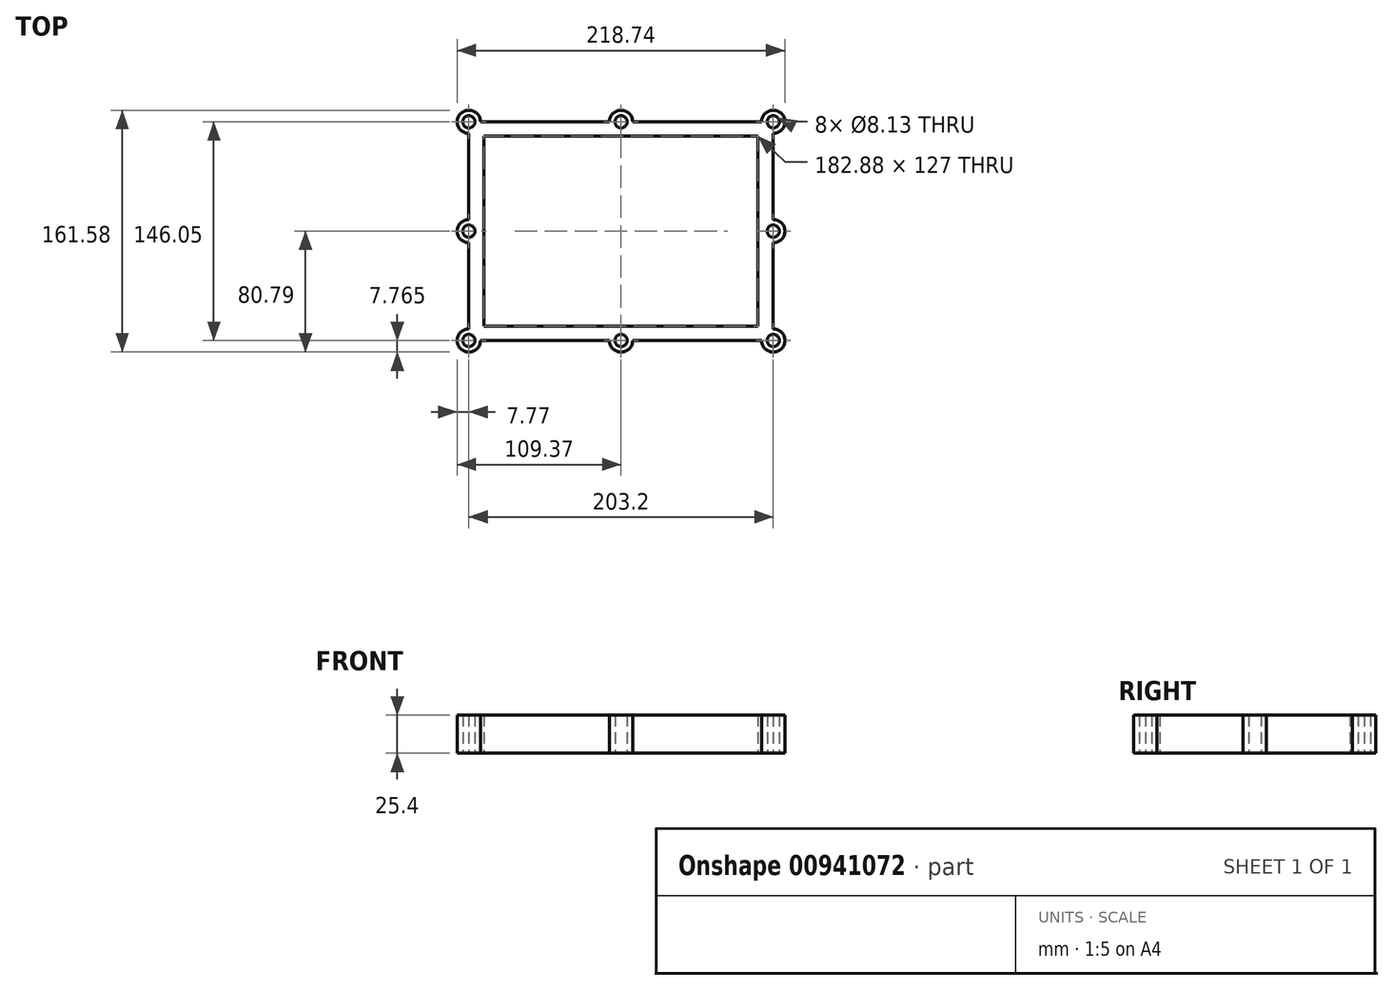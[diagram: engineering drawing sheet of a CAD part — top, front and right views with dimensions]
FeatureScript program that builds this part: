
annotation { "Feature Type Name" : "Feature", "Feature Type Description" : "" }
export const myFeature = defineFeature(function(context is Context, id is Id, definition is map)
    precondition{}
    {
        {
            var Q0;
            Q0=qCreatedBy(makeId("Top.planeOp"),FACE);
            var sketch = newSketch(context, id + "F0", { "sketchPlane" : qUnion([Q0])});
            skLineSegment(sketch, "E0.bottom", {"start": v(-101.6, 73.03) * mm, "end": v(101.6, 73.03) * mm});
            skLineSegment(sketch, "E0.top", {"start": v(-101.6, -73.03) * mm, "end": v(101.6, -73.03) * mm});
            skLineSegment(sketch, "E0.left", {"start": v(-101.6, 73.02) * mm, "end": v(-101.6, -73.03) * mm});
            skLineSegment(sketch, "E0.right", {"start": v(101.6, 73.03) * mm, "end": v(101.6, -73.02) * mm});
            skLineSegment(sketch, "E1", {"start": v(-101.6, 0) * mm, "end": v(101.6, 0) * mm, "construction": true});
            skLineSegment(sketch, "E2", {"start": v(0, 73.03) * mm, "end": v(0, -73.03) * mm, "construction": true});
            skPoint(sketch, "E2.startSnap0", {"position": v(0, 73.02) * mm});
            skCircle(sketch, "E3", {"center": v(101.6, -73.03) * mm, "radius": 7.77 * mm});
            skCircle(sketch, "E4", {"center": v(101.6, -73.03) * mm, "radius": 4.06 * mm});
            skCircle(sketch, "E5", {"center": v(101.6, 0) * mm, "radius": 7.77 * mm});
            skCircle(sketch, "E6", {"center": v(101.6, 0) * mm, "radius": 4.06 * mm});
            skCircle(sketch, "E7", {"center": v(101.6, 73.03) * mm, "radius": 7.77 * mm});
            skCircle(sketch, "E8", {"center": v(101.6, 73.03) * mm, "radius": 4.06 * mm});
            skCircle(sketch, "E9", {"center": v(0, 73.03) * mm, "radius": 7.77 * mm});
            skCircle(sketch, "E10", {"center": v(0, 73.03) * mm, "radius": 4.06 * mm});
            skCircle(sketch, "E11", {"center": v(-101.6, 73.03) * mm, "radius": 7.77 * mm});
            skCircle(sketch, "E12", {"center": v(-101.6, 73.03) * mm, "radius": 4.06 * mm});
            skCircle(sketch, "E13", {"center": v(-101.6, 0) * mm, "radius": 7.77 * mm});
            skCircle(sketch, "E14", {"center": v(-101.6, 0) * mm, "radius": 4.06 * mm});
            skCircle(sketch, "E15", {"center": v(-101.6, -73.03) * mm, "radius": 7.77 * mm});
            skCircle(sketch, "E16", {"center": v(-101.6, -73.03) * mm, "radius": 4.06 * mm});
            skCircle(sketch, "E17", {"center": v(0, -73.03) * mm, "radius": 7.77 * mm});
            skCircle(sketch, "E18", {"center": v(0, -73.03) * mm, "radius": 4.06 * mm});
            skLineSegment(sketch, "E19", {"start": v(-91.44, -63.5) * mm, "end": v(91.44, -63.5) * mm});
            skLineSegment(sketch, "E20", {"start": v(91.44, 63.5) * mm, "end": v(91.44, -63.5) * mm});
            skLineSegment(sketch, "E21", {"start": v(-91.44, 63.5) * mm, "end": v(-91.44, -63.5) * mm});
            skLineSegment(sketch, "E22", {"start": v(91.44, -63.5) * mm, "end": v(91.44, -73.03) * mm, "construction": true});
            skLineSegment(sketch, "E23", {"start": v(91.44, -24.5) * mm, "end": v(101.6, -24.5) * mm, "construction": true});
            skLineSegment(sketch, "E24", {"start": v(-91.44, 63.5) * mm, "end": v(91.44, 63.5) * mm});
            skSolve(sketch);
        }
        {
            var Q0;
            Q0=qSketchRegion(id+"F0",true);
            extrude(context, id + "F1", {"entities" : qUnion([Q0]), "depth" : 25.4 * mm, "offsetDistance" : 25.4 * mm});
        }
    });
